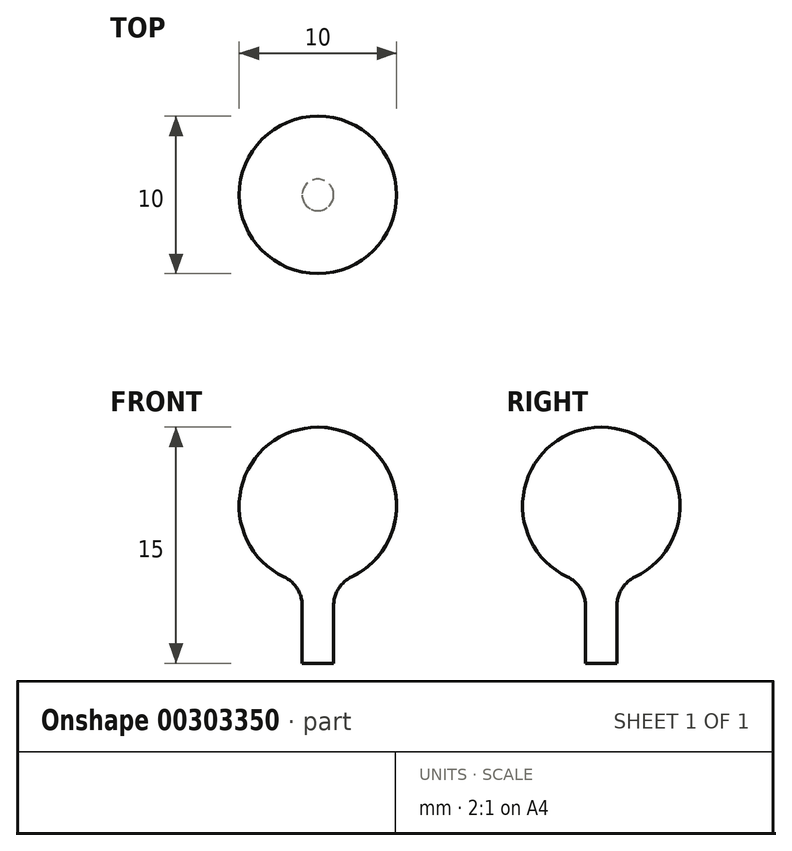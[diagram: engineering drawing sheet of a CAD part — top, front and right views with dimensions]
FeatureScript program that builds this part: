
annotation { "Feature Type Name" : "Feature", "Feature Type Description" : "" }
export const myFeature = defineFeature(function(context is Context, id is Id, definition is map)
    precondition{}
    {
        {
            var Q0;
            Q0=qCreatedBy(makeId("Front.planeOp"),FACE);
            var sketch = newSketch(context, id + "F0", { "sketchPlane" : qUnion([Q0])});
            skArc(sketch, "E0", {"start": v(1, -4.9) * mm, "mid": v(4.97, 0.5) * mm, "end": v(0, 5) * mm});
            skLineSegment(sketch, "E1.bottom", {"start": v(1, -10) * mm, "end": v(0, -10) * mm});
            skLineSegment(sketch, "E1.left", {"start": v(1, -10) * mm, "end": v(1, -4.9) * mm});
            skPoint(sketch, "E1.top.start.orphan", {"position": v(1, 10) * mm});
            skPoint(sketch, "E2.orphan", {"position": v(-1, 10) * mm});
            skPoint(sketch, "E3.orphan", {"position": v(0, -10) * mm});
            skPoint(sketch, "E4.start.orphan", {"position": v(0, 5) * mm});
            skLineSegment(sketch, "E5", {"start": v(0, 5) * mm, "end": v(0, 0) * mm});
            skPoint(sketch, "E6.orphan", {"position": v(-1, -10) * mm});
            skLineSegment(sketch, "E7", {"start": v(0, 0) * mm, "end": v(0, -10) * mm});
            skLineSegment(sketch, "E8", {"start": v(0, -12.95) * mm, "end": v(0, 10.06) * mm, "construction": true});
            skSolve(sketch);
        }
        {
            var Q0;
            Q0=makeQuery(id+"F0.imprint","IMPRINT",FACE,{"disambiguationData":[TD([[makeQuery(id+"F0.imprint","IMPRINT",EDGE,{"derivedFrom":sQuery(id+"F0.wireOp",EDGE,"E0")}),1.0]])]});
            var Q1;
            Q1=sQuery(id+"F0.wireOp",EDGE,"E0");
            var Q2;
            Q2=sQuery(id+"F0.wireOp",EDGE,"E8");
            revolve(context, id + "F1", {"entities" : qUnion([Q0]), "surfaceEntities" : qUnion([Q1]), "axis" : qUnion([Q2]), "revolveType" : RevolveType.FULL});
        }
        {
            var Q0;
            Q0=makeQuery(id+"F1.opRevolve","SWEPT_EDGE",EDGE,{"disambiguationData":[OSD([sQuery(id+"F0.wireOp",EDGE,"E0"),sQuery(id+"F0.wireOp",EDGE,"E1.left")])]});
            fillet(context, id + "F2", {"entities" : qUnion([Q0]), "radius" : 2 * mm, "tangentPropagation" : true, "allowEdgeOverflow" : false});
        }
    });
